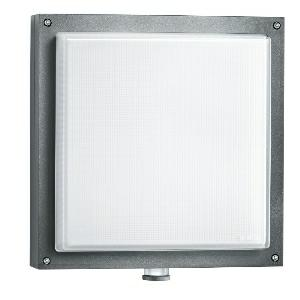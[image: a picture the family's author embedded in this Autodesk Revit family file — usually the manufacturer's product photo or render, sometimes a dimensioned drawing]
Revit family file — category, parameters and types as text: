
# Revit family: l_690_led_053000
name_source: partatom
category: Leuchten
revit_build: Autodesk Revit 2016 (Build: 20190508_0715(x64)
units: mm (PartAtom-declared; Revit-internal decimal feet)

## family parameters
Basisbauteil = Fläche
Beim Laden mit Abzugskörper schneiden = Nein
Bemaßung runder Anschluss = Durchmesser verwenden
Gemeinsam genutzt = Nein
Lichtquelle = Nein
Raumberechnungspunkt = Nein
Teiletyp = Normal

## types (1)
- L 690 LED (1 x , 753 lm, 3000 K)
    Beschreibung = Dimensions (L x W x H): 104 x 291 x 303 mm; Mains power supply: 220 – 240 V / 50 Hz; Mounting height max.: 2,50 m; Sensor Technology: passive infrared; Output: 9 W; Interconnection: Yes; Slave modeselectable: No; Luminous flux: 753 lm; Colour temperature: 3000 K; Colour variation LED: SDCM3; Colour Rendering Index CRI: 80-89; With lamp: Yes, STEINEL LED system; Lamp: LED cannot be replaced; LED life expectancy (max. °C): 50000 h; Base: without; LED cooling system: Passive Thermo Control; With motion detector: Yes; Detection angle: 360 °; Sneak-by guard: Yes; Capability of masking out individual segments: Yes; Electronic scalability: No; Mechanical scalability: No; Reach, radial: r = 1.5 m (7 m²); Reach, tangential: r = 7 m (154 m²); Photo-cell controller: Yes; Twilight setting: 2 – 1000 lx; Time setting: 5 sec – 15 min; Basic light level function: Yes; Basic light level function time: 10/30 min, all night; Functions: 4 programme settings geared to practical needs, can be selected on removable sensor module; Soft light start: Yes; Continuous light: selectable, 4h; Impact resistance: IK07; IP-rating: IP44; Protection class: II; Ambient temperature: -10 – 50 °C; Housing material: Aluminium; Cover material: Plastic, opal; Manufacturer's Warranty: 5 years; includes sheet of self-adhesive numbers: Yes; Settings via: Potentiometers; Cover material: shrouds; Version: PMMA anthracite; PU1, EAN: 4007841053000
    Color Rendering = 80-89
    Color Temperature = 3000 K
    Frequency = 50 Hz
    Height = 303 mm
    Hersteller = Steinel
    Lamp Light Flux = 753 lm
    Lamp count = 1
    Lampe = 1 x
    Length = 104 mm  [stored 0.341207 ft]
    Luminous efficacy = 0 lm/W
    ModVariant = Nein
    Modell = 053000
    Mounting Type = Surface mounted
    Number of Poles = 1
    OnlyDefault = Ja
    Power Factor = 1
    Product Name = L 690 LED
    Product group = Sensor-switched indoor light
    ProductGroupID = 30
    Protection Class = Protection class II
    Protection Degree = IP 34
    RlxData = <blob elided: 61681 chars, md5=dfafa414>
    Scheinlast = 9 VA
    Socket = socket
    Standby Power = 0 W
    System Light Flux = 0 lm
    System Power = 9 W
    Typenbild = produkt1_053000.jpg
    Typenkommentare = Product without accessories
    URL = http://relux.com
    VarID = ---
    Voltage = 0 V
    Vorgabe-Ansicht = 1800 mm
    Weight = 0.00 kg
    Width = 291 mm

note: [stored X ft] marks values corroborated as IEEE doubles in the binary element streams (Revit-internal decimal feet)

## geometry (parser evidence)
native form markers: Blend x4, Sweep x11
no freeform markers — native parametric forms only
